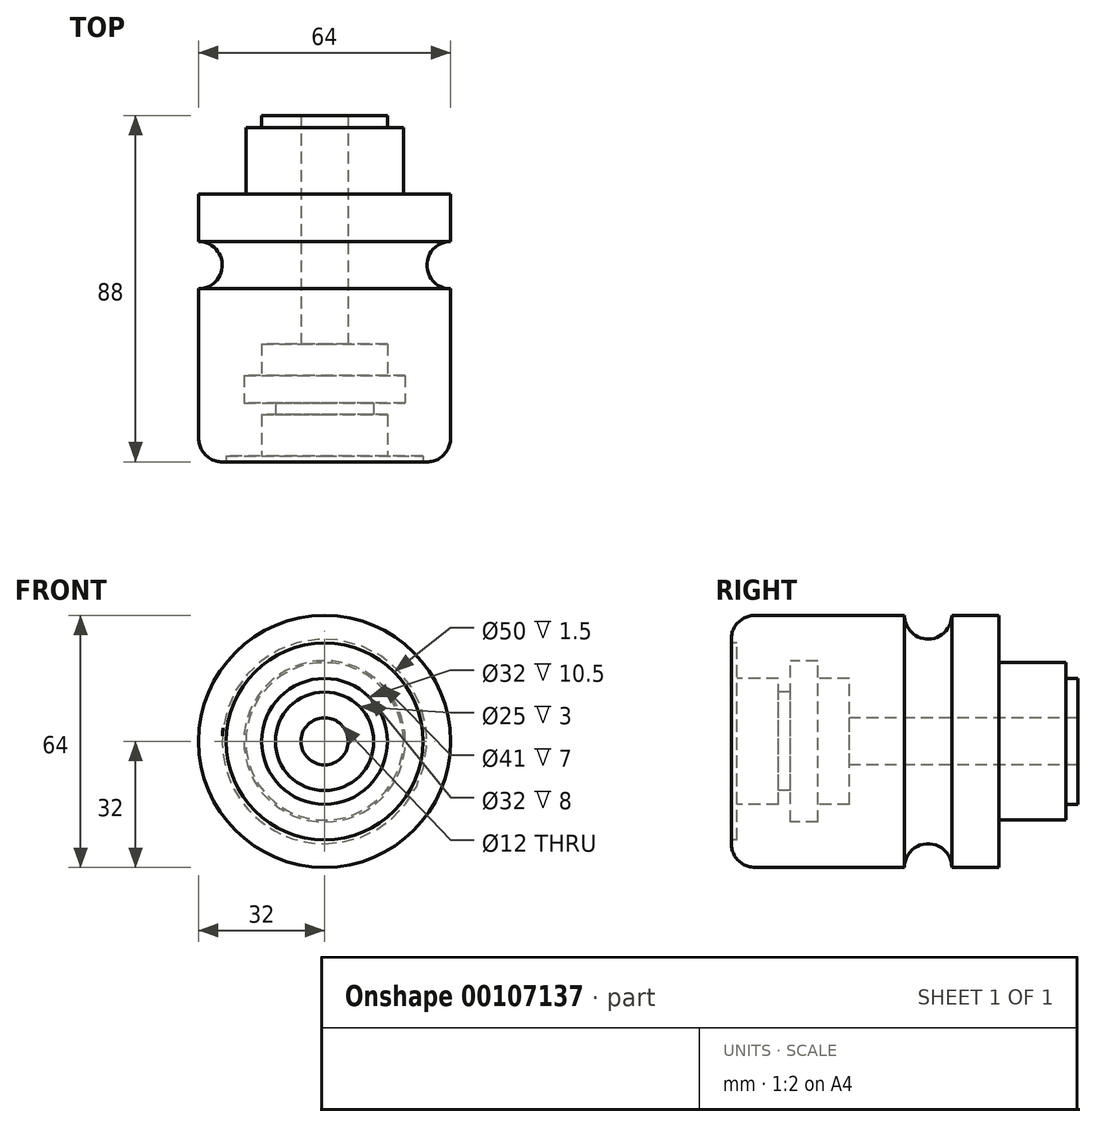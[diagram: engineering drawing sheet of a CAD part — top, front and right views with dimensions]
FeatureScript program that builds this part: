
annotation { "Feature Type Name" : "Feature", "Feature Type Description" : "" }
export const myFeature = defineFeature(function(context is Context, id is Id, definition is map)
    precondition{}
    {
        {
            var Q0;
            Q0=qCreatedBy(makeId("Right.planeOp"),FACE);
            var sketch = newSketch(context, id + "F0", { "sketchPlane" : qUnion([Q0])});
            skLineSegment(sketch, "E0", {"start": v(88, 6) * mm, "end": v(88, 16) * mm});
            skLineSegment(sketch, "E1", {"start": v(88, 16) * mm, "end": v(85, 16) * mm});
            skLineSegment(sketch, "E2", {"start": v(85, 16) * mm, "end": v(85, 20) * mm});
            skLineSegment(sketch, "E3", {"start": v(85, 20) * mm, "end": v(68, 20) * mm});
            skLineSegment(sketch, "E4", {"start": v(68, 20) * mm, "end": v(68, 32) * mm});
            skLineSegment(sketch, "E5", {"start": v(68, 32) * mm, "end": v(56, 32) * mm});
            skLineSegment(sketch, "E6", {"start": v(44, 32) * mm, "end": v(0, 32) * mm});
            skLineSegment(sketch, "E7", {"start": v(0, 32) * mm, "end": v(0, 25) * mm});
            skLineSegment(sketch, "E8", {"start": v(0, 25) * mm, "end": v(1.5, 25) * mm});
            skLineSegment(sketch, "E9", {"start": v(1.5, 25) * mm, "end": v(1.5, 16) * mm});
            skLineSegment(sketch, "E10", {"start": v(1.5, 16) * mm, "end": v(12, 16) * mm});
            skLineSegment(sketch, "E11", {"start": v(30, 6) * mm, "end": v(88, 6) * mm});
            skLineSegment(sketch, "E12", {"start": v(12, 16) * mm, "end": v(12, 12.5) * mm});
            skLineSegment(sketch, "E13", {"start": v(12, 12.5) * mm, "end": v(15, 12.5) * mm});
            skLineSegment(sketch, "E14", {"start": v(15, 12.5) * mm, "end": v(15, 20.5) * mm});
            skLineSegment(sketch, "E15", {"start": v(15, 20.5) * mm, "end": v(22, 20.5) * mm});
            skLineSegment(sketch, "E16", {"start": v(22, 20.5) * mm, "end": v(22, 16) * mm});
            skLineSegment(sketch, "E17", {"start": v(22, 16) * mm, "end": v(30, 16) * mm});
            skLineSegment(sketch, "E18", {"start": v(30, 16) * mm, "end": v(30, 6) * mm});
            skLineSegment(sketch, "E19", {"start": v(0, 0) * mm, "end": v(98.5, 0) * mm, "construction": true});
            skArc(sketch, "E20", {"start": v(44, 32) * mm, "mid": v(50, 26) * mm, "end": v(56, 32) * mm});
            skSolve(sketch);
        }
        {
            var Q0;
            Q0=makeQuery(id+"F0.imprint","IMPRINT",FACE,{"disambiguationData":[TD([[makeQuery(id+"F0.imprint","IMPRINT",EDGE,{"derivedFrom":sQuery(id+"F0.wireOp",EDGE,"E0")}),1.0]])]});
            var Q1;
            Q1=sQuery(id+"F0.wireOp",EDGE,"E19");
            revolve(context, id + "F1", {"entities" : qUnion([Q0]), "axis" : qUnion([Q1]), "revolveType" : RevolveType.FULL});
        }
        {
            var Q0;
            Q0=makeQuery(id+"F1.opRevolve","SWEPT_EDGE",EDGE,{"disambiguationData":[OSD([sQuery(id+"F0.wireOp",EDGE,"E6"),sQuery(id+"F0.wireOp",EDGE,"E7")])]});
            fillet(context, id + "F2", {"entities" : qUnion([Q0]), "radius" : 6 * mm, "tangentPropagation" : true, "allowEdgeOverflow" : false});
        }
    });
